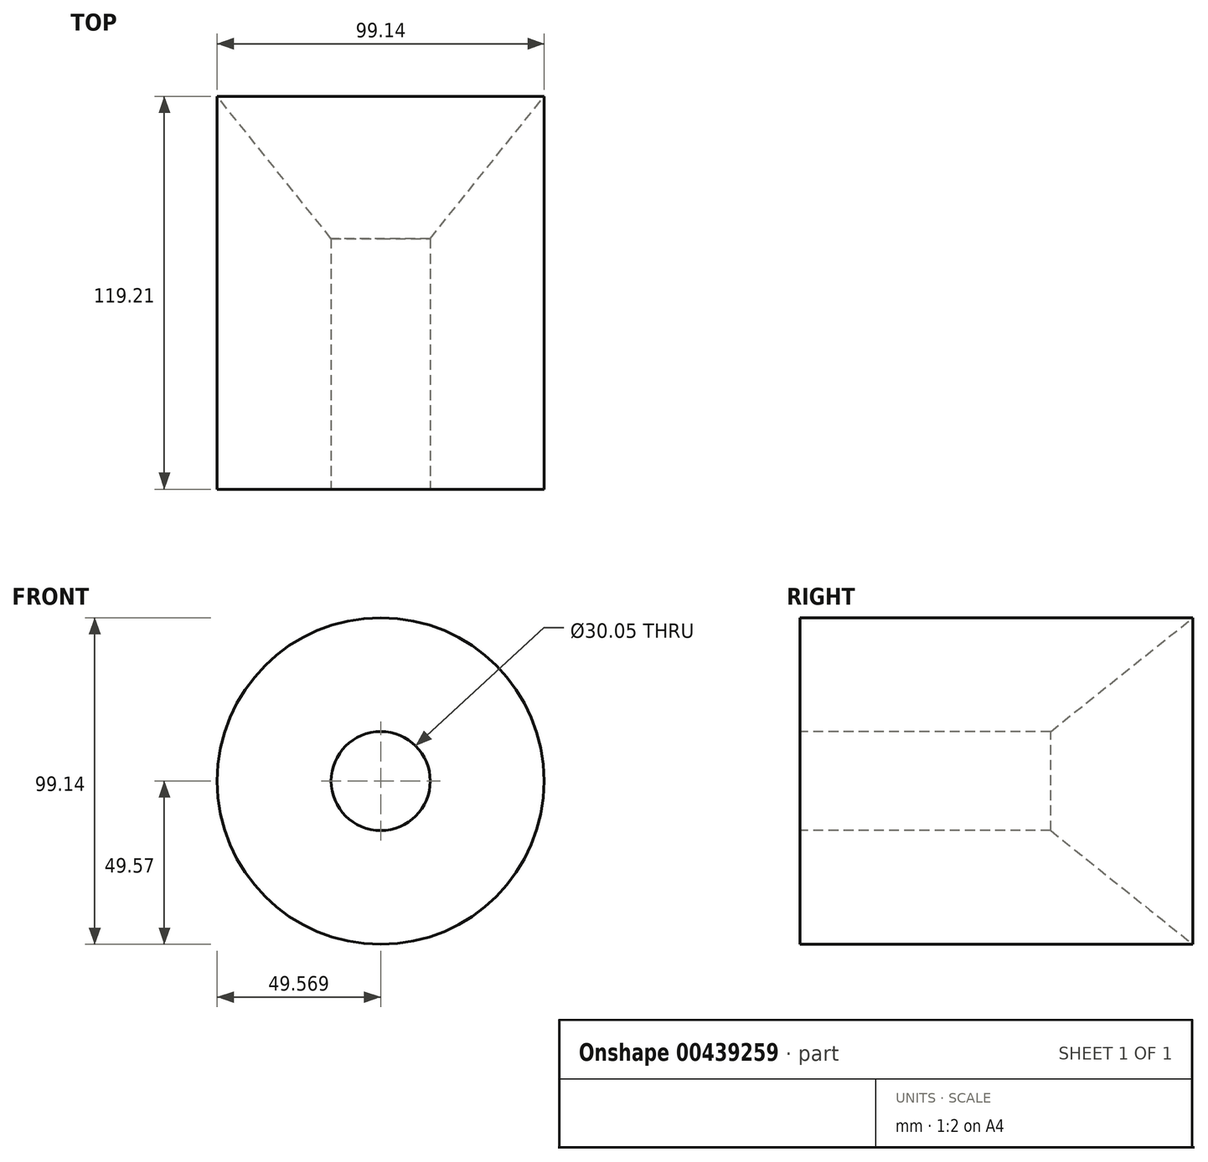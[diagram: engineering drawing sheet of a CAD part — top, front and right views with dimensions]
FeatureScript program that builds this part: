
annotation { "Feature Type Name" : "Feature", "Feature Type Description" : "" }
export const myFeature = defineFeature(function(context is Context, id is Id, definition is map)
    precondition{}
    {
        {
            var Q0;
            Q0=qCreatedBy(makeId("Top.planeOp"),FACE);
            var sketch = newSketch(context, id + "F0", { "sketchPlane" : qUnion([Q0])});
            skLineSegment(sketch, "E0", {"start": v(-140.25, -46.73) * mm, "end": v(-140.25, 72.48) * mm});
            skLineSegment(sketch, "E1", {"start": v(-140.25, 72.48) * mm, "end": v(-105.7, 29.34) * mm});
            skLineSegment(sketch, "E2", {"start": v(-105.7, 29.34) * mm, "end": v(-105.7, -46.73) * mm});
            skLineSegment(sketch, "E3", {"start": v(-105.7, -46.73) * mm, "end": v(-140.25, -46.73) * mm});
            skLineSegment(sketch, "E4", {"start": v(-90.68, -66.43) * mm, "end": v(-90.68, 56.68) * mm, "construction": true});
            skSolve(sketch);
        }
        {
            var Q0;
            Q0=makeQuery(id+"F0.imprint","IMPRINT",FACE,{"disambiguationData":[TD([[makeQuery(id+"F0.imprint","IMPRINT",EDGE,{"derivedFrom":sQuery(id+"F0.wireOp",EDGE,"E0")}),-1.0]])]});
            var Q1;
            Q1=sQuery(id+"F0.wireOp",EDGE,"E4");
            revolve(context, id + "F1", {"entities" : qUnion([Q0]), "axis" : qUnion([Q1]), "revolveType" : RevolveType.FULL});
        }
    });
